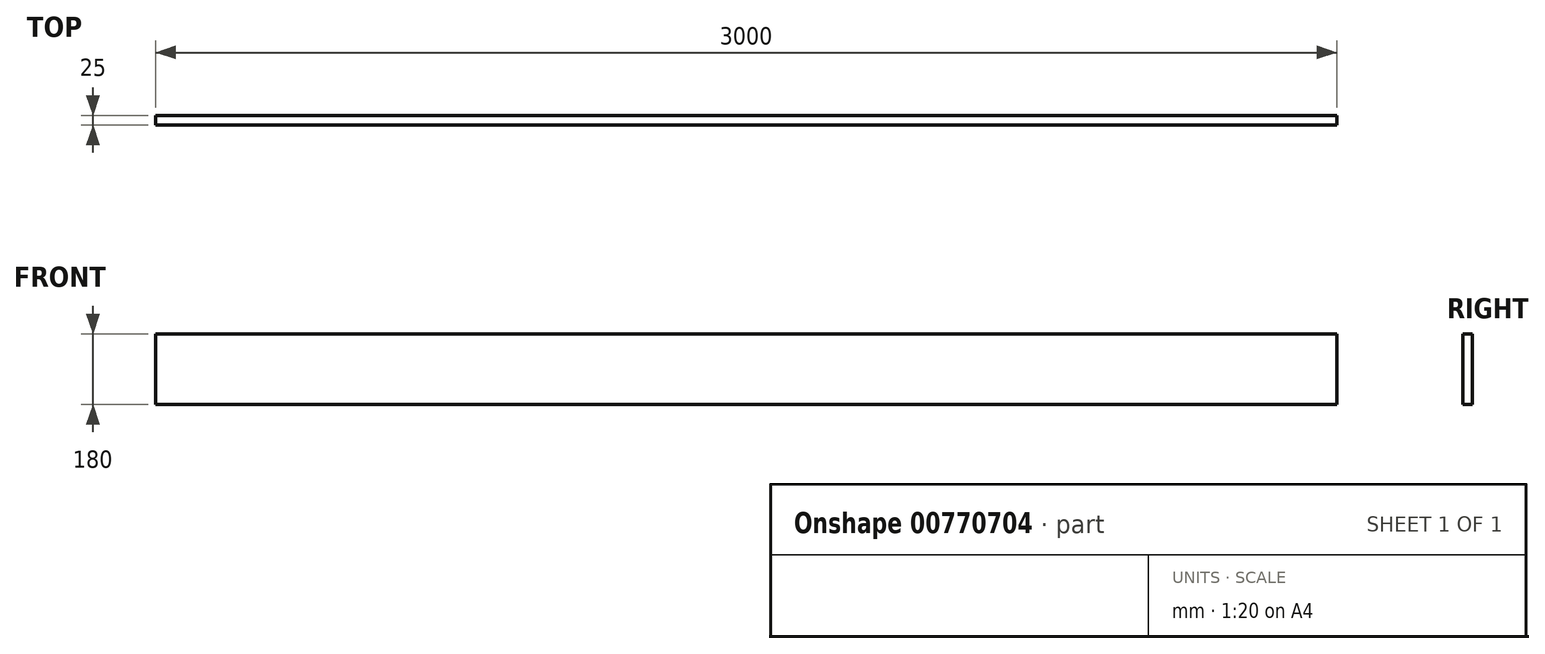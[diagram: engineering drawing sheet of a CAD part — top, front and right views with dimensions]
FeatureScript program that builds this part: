
annotation { "Feature Type Name" : "Feature", "Feature Type Description" : "" }
export const myFeature = defineFeature(function(context is Context, id is Id, definition is map)
    precondition{}
    {
        {
            var Q0;
            Q0=qCreatedBy(makeId("Front.planeOp"),FACE);
            var sketch = newSketch(context, id + "F0", { "sketchPlane" : qUnion([Q0])});
            skLineSegment(sketch, "E0.bottom", {"start": v(-125.21, 93.31) * mm, "end": v(2874.79, 93.31) * mm});
            skLineSegment(sketch, "E0.top", {"start": v(-125.21, -86.69) * mm, "end": v(2874.79, -86.69) * mm});
            skLineSegment(sketch, "E0.left", {"start": v(-125.21, 93.31) * mm, "end": v(-125.21, -86.69) * mm});
            skLineSegment(sketch, "E0.right", {"start": v(2874.79, 93.31) * mm, "end": v(2874.79, -86.69) * mm});
            skSolve(sketch);
        }
        {
            var Q0;
            Q0 = qSketchRegion(id + "F0", true);
            extrude(context, id + "F1", {"entities" : qUnion([Q0]), "depth" : 25 * mm, "offsetDistance" : 25 * mm});
        }
    });
